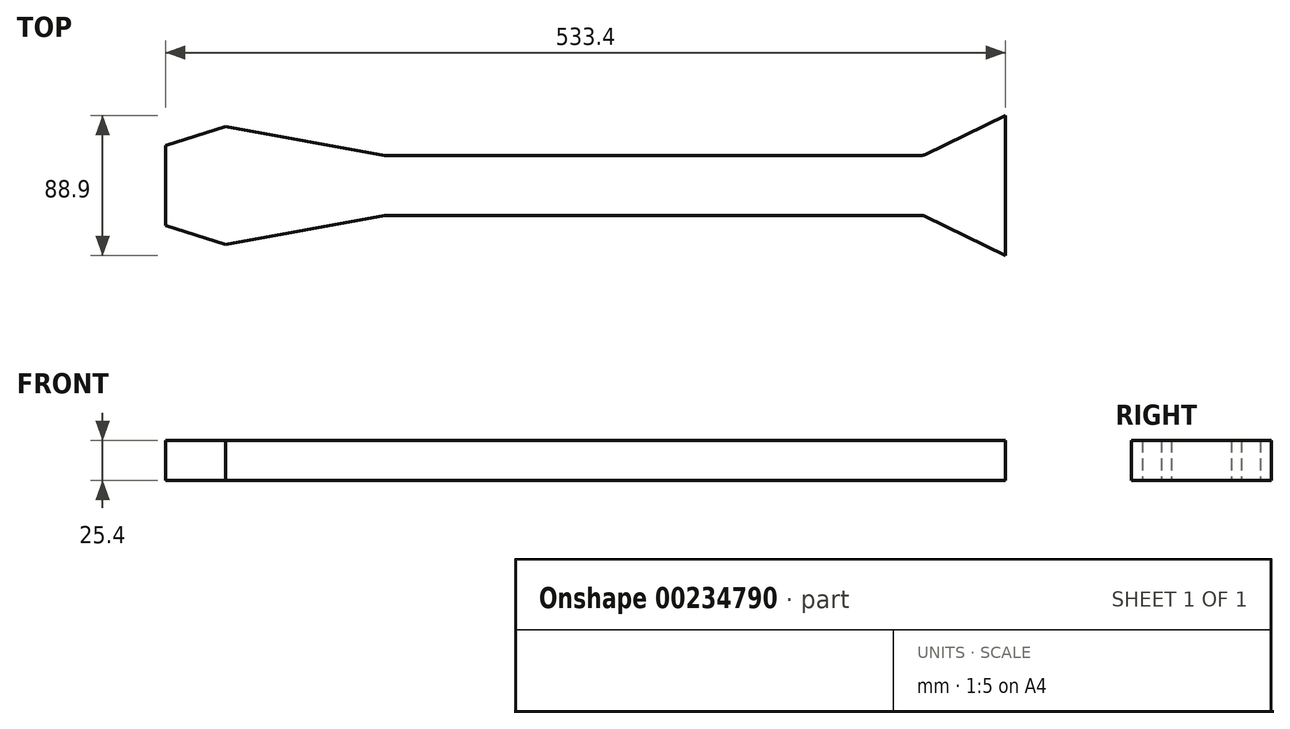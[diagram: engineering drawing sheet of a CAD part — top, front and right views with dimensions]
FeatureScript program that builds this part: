
annotation { "Feature Type Name" : "Feature", "Feature Type Description" : "" }
export const myFeature = defineFeature(function(context is Context, id is Id, definition is map)
    precondition{}
    {
        {
            var Q0;
            Q0=qCreatedBy(makeId("Top.planeOp"),FACE);
            var sketch = newSketch(context, id + "F0", { "sketchPlane" : qUnion([Q0])});
            skLineSegment(sketch, "E0.bottom", {"start": v(0, 0) * mm, "end": v(914.4, 0) * mm});
            skLineSegment(sketch, "E0.top", {"start": v(0, 88.9) * mm, "end": v(914.4, 88.9) * mm});
            skLineSegment(sketch, "E0.left", {"start": v(0, 0) * mm, "end": v(0, 88.9) * mm});
            skLineSegment(sketch, "E0.right", {"start": v(914.4, 0) * mm, "end": v(914.4, 88.9) * mm});
            skLineSegment(sketch, "E1", {"start": v(139.7, 88.9) * mm, "end": v(139.7, 0) * mm, "construction": true});
            skLineSegment(sketch, "E2", {"start": v(787.4, 88.9) * mm, "end": v(787.4, 0) * mm, "construction": true});
            skLineSegment(sketch, "E3", {"start": v(176.05, 88.9) * mm, "end": v(176.05, 0) * mm, "construction": true});
            skLineSegment(sketch, "E4", {"start": v(210.36, 88.9) * mm, "end": v(210.36, 0) * mm, "construction": true});
            skLineSegment(sketch, "E5", {"start": v(242.75, 88.9) * mm, "end": v(242.75, 0) * mm, "construction": true});
            skLineSegment(sketch, "E6", {"start": v(273.33, 88.9) * mm, "end": v(273.33, 0) * mm, "construction": true});
            skLineSegment(sketch, "E7", {"start": v(302.18, 88.9) * mm, "end": v(302.18, 0) * mm, "construction": true});
            skLineSegment(sketch, "E8", {"start": v(329.41, 88.9) * mm, "end": v(329.41, 0) * mm, "construction": true});
            skLineSegment(sketch, "E9", {"start": v(355.12, 88.9) * mm, "end": v(355.12, 0) * mm, "construction": true});
            skLineSegment(sketch, "E10", {"start": v(379.37, 88.9) * mm, "end": v(379.37, 0) * mm, "construction": true});
            skLineSegment(sketch, "E11", {"start": v(402.29, 88.9) * mm, "end": v(402.29, 0) * mm, "construction": true});
            skLineSegment(sketch, "E12", {"start": v(423.9, 88.9) * mm, "end": v(423.9, 0) * mm, "construction": true});
            skLineSegment(sketch, "E13", {"start": v(444.3, 88.9) * mm, "end": v(444.3, 0) * mm, "construction": true});
            skLineSegment(sketch, "E14", {"start": v(463.55, 88.9) * mm, "end": v(463.55, 0) * mm, "construction": true});
            skLineSegment(sketch, "E15", {"start": v(481.23, 88.9) * mm, "end": v(481.23, 0) * mm, "construction": true});
            skLineSegment(sketch, "E16", {"start": v(498.88, 88.9) * mm, "end": v(498.88, 0) * mm, "construction": true});
            skLineSegment(sketch, "E17", {"start": v(515.09, 88.9) * mm, "end": v(515.09, 0) * mm, "construction": true});
            skLineSegment(sketch, "E18", {"start": v(530.35, 88.9) * mm, "end": v(530.35, 0) * mm, "construction": true});
            skLineSegment(sketch, "E19", {"start": v(544.78, 88.9) * mm, "end": v(544.78, 0) * mm, "construction": true});
            skLineSegment(sketch, "E20", {"start": v(139.7, 63.5) * mm, "end": v(787.4, 63.5) * mm});
            skLineSegment(sketch, "E21", {"start": v(787.4, 25.4) * mm, "end": v(139.7, 25.4) * mm});
            skLineSegment(sketch, "E22", {"start": v(139.7, 63.5) * mm, "end": v(38.1, 81.97) * mm});
            skLineSegment(sketch, "E23", {"start": v(139.7, 25.4) * mm, "end": v(38.1, 6.93) * mm});
            skLineSegment(sketch, "E24", {"start": v(533.4, 88.9) * mm, "end": v(533.4, 0) * mm});
            skLineSegment(sketch, "E25", {"start": v(533.4, 0) * mm, "end": v(481.23, 25.4) * mm});
            skLineSegment(sketch, "E26", {"start": v(481.23, 63.5) * mm, "end": v(533.4, 88.9) * mm});
            skLineSegment(sketch, "E27", {"start": v(38.1, 81.97) * mm, "end": v(38.1, 6.93) * mm, "construction": true});
            skLineSegment(sketch, "E28", {"start": v(38.1, 6.93) * mm, "end": v(0, 19.05) * mm});
            skLineSegment(sketch, "E29", {"start": v(38.1, 81.97) * mm, "end": v(0, 69.85) * mm});
            skLineSegment(sketch, "E30", {"start": v(0, 44.45) * mm, "end": v(633.94, 44.45) * mm, "construction": true});
            skPoint(sketch, "E30.endSnap0", {"position": v(544.78, 44.45) * mm});
            skSolve(sketch);
        }
        {
            var Q0;
            {var subQ7=sQuery(id+"F0.wireOp",EDGE,"E22");Q0=makeQuery(id+"F0.imprint","IMPRINT",FACE,{"disambiguationData":[TD([[makeQuery(id+"F0.imprint","IMPRINT",EDGE,{"derivedFrom":subQ7}),1.0]])]});}
            var Q1;
            {var subQ0=sQuery(id+"F0.wireOp",EDGE,"E25");Q1=makeQuery(id+"F0.imprint","IMPRINT",FACE,{"disambiguationData":[TD([[makeQuery(id+"F0.imprint","IMPRINT",EDGE,{"derivedFrom":subQ0}),-1.0]])]});}
            var Q2;
            {var subQ0=sQuery(id+"F0.wireOp",EDGE,"E26");Q2=makeQuery(id+"F0.imprint","IMPRINT",FACE,{"disambiguationData":[TD([[makeQuery(id+"F0.imprint","IMPRINT",EDGE,{"derivedFrom":subQ0}),-1.0]])]});}
            extrude(context, id + "F1", {"entities" : qUnion([Q0, Q1, Q2]), "depth" : 25.4 * mm});
        }
        {
            var Q0;
            Q0=makeQuery(id+"F1.opExtrude","SWEPT_EDGE",EDGE,{"disambiguationData":[OSD([sQuery(id+"F0.wireOp",EDGE,"E20"),sQuery(id+"F0.wireOp",EDGE,"E22")])]});
            var Q1;
            Q1=makeQuery(id+"F1.opExtrude","SWEPT_EDGE",EDGE,{"disambiguationData":[OSD([sQuery(id+"F0.wireOp",EDGE,"E20"),sQuery(id+"F0.wireOp",EDGE,"E26")])]});
            var Q2;
            Q2=makeQuery(id+"F1.opExtrude","SWEPT_EDGE",EDGE,{"disambiguationData":[OSD([sQuery(id+"F0.wireOp",EDGE,"E21"),sQuery(id+"F0.wireOp",EDGE,"E23")])]});
            var Q3;
            Q3=makeQuery(id+"F1.opExtrude","SWEPT_EDGE",EDGE,{"disambiguationData":[OSD([sQuery(id+"F0.wireOp",EDGE,"E21"),sQuery(id+"F0.wireOp",EDGE,"E25")])]});
            fillet(context, id + "F2", {"entities" : qUnion([Q0, Q1, Q2, Q3]), "radius" : 6.35 * mm, "tangentPropagation" : true, "allowEdgeOverflow" : false});
        }
    });
